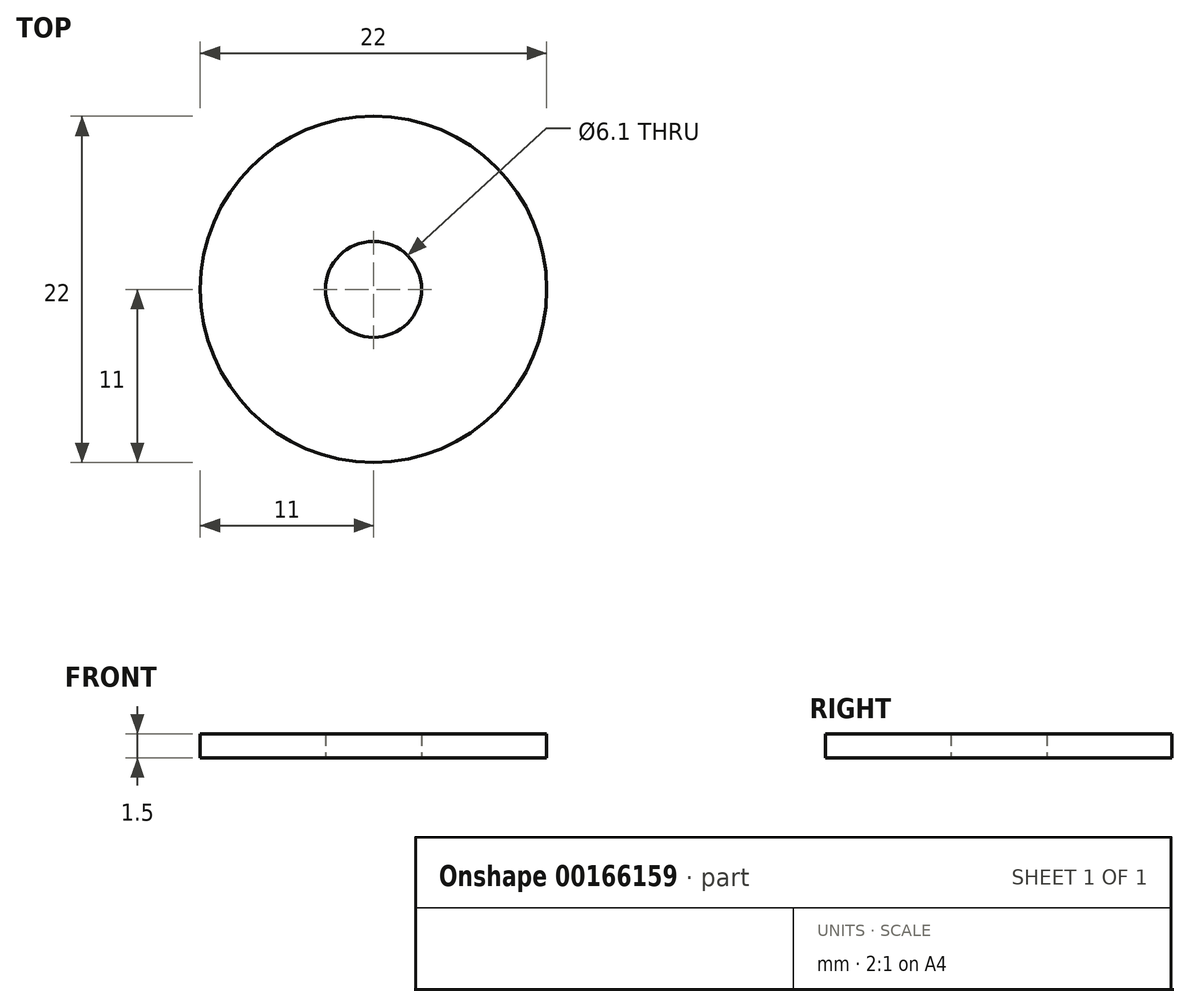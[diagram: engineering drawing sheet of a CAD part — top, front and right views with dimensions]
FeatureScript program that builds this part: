
annotation { "Feature Type Name" : "Feature", "Feature Type Description" : "" }
export const myFeature = defineFeature(function(context is Context, id is Id, definition is map)
    precondition{}
    {
        {
            var Q0;
            Q0=qCreatedBy(makeId("Top.planeOp"),FACE);
            var sketch = newSketch(context, id + "F0", { "sketchPlane" : qUnion([Q0])});
            skCircle(sketch, "E0", {"center": v(0, 0) * mm, "radius": 11 * mm});
            skCircle(sketch, "E1", {"center": v(0, 0) * mm, "radius": 3.05 * mm});
            skSolve(sketch);
        }
        {
            var Q0;
            Q0 = qSketchRegion(id + "F0", true);
            extrude(context, id + "F1", {"entities" : qUnion([Q0]), "depth" : 1.5 * mm});
        }
    });
